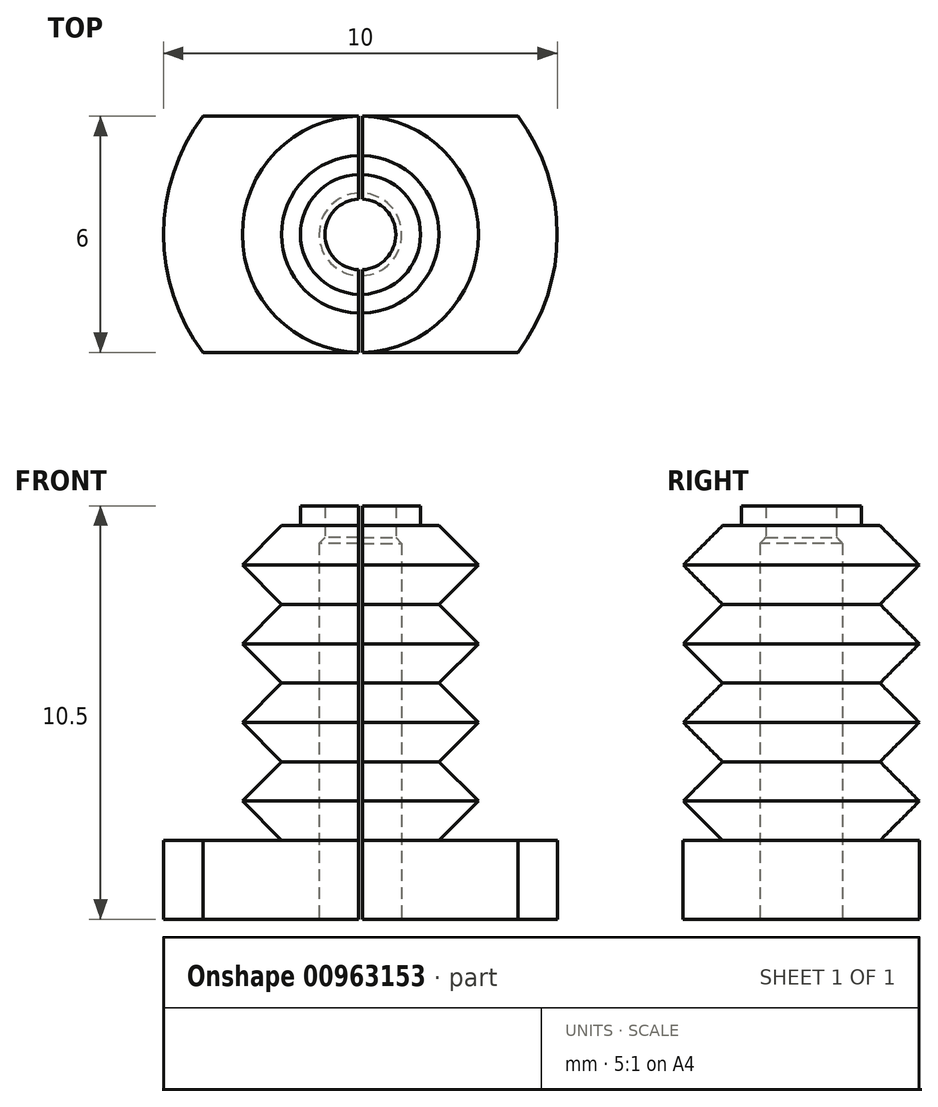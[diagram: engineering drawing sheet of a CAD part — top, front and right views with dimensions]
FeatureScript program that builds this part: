
annotation { "Feature Type Name" : "Feature", "Feature Type Description" : "" }
export const myFeature = defineFeature(function(context is Context, id is Id, definition is map)
    precondition{}
    {
        {
            var Q0;
            Q0=qCreatedBy(makeId("Top.planeOp"),FACE);
            var sketch = newSketch(context, id + "F0", { "sketchPlane" : qUnion([Q0])});
            skArc(sketch, "E0", {"start": v(0.12, 1.04) * mm, "mid": v(-1.05, 0) * mm, "end": v(0.12, -1.04) * mm});
            skArc(sketch, "E1", {"start": v(-0.16, 2) * mm, "mid": v(-2, 0) * mm, "end": v(-0.16, -2) * mm});
            skArc(sketch, "E2.trimOffspring", {"start": v(0.12, -1.04) * mm, "mid": v(1.05, 0) * mm, "end": v(0.12, 1.04) * mm});
            skArc(sketch, "E3.trimOffspring", {"start": v(-0.16, -2) * mm, "mid": v(2, 0) * mm, "end": v(-0.16, 2) * mm});
            skSolve(sketch);
        }
        {
            var Q0;
            Q0=makeQuery(id+"F0.imprint","IMPRINT",FACE,{"disambiguationData":[TD([[makeQuery(id+"F0.imprint","IMPRINT",EDGE,{"derivedFrom":sQuery(id+"F0.wireOp",EDGE,"E0")}),-1.0]])]});
            extrude(context, id + "F1", {"entities" : qUnion([Q0]), "depth" : 10 * mm, "offsetDistance" : 25 * mm});
        }
        {
            var Q0;
            Q0=qCreatedBy(makeId("Right.planeOp"),FACE);
            var sketch = newSketch(context, id + "F2", { "sketchPlane" : qUnion([Q0])});
            skLineSegment(sketch, "E4", {"start": v(-2, 8) * mm, "end": v(-3, 7) * mm});
            skLineSegment(sketch, "E5", {"start": v(-3, 7) * mm, "end": v(-2, 6) * mm});
            skLineSegment(sketch, "E6", {"start": v(-2, 6) * mm, "end": v(-3, 5) * mm});
            skLineSegment(sketch, "E7", {"start": v(-3, 5) * mm, "end": v(-2, 4) * mm});
            skLineSegment(sketch, "E8", {"start": v(-2, 4) * mm, "end": v(-3, 3) * mm});
            skLineSegment(sketch, "E9", {"start": v(-3, 3) * mm, "end": v(-2, 2) * mm});
            skLineSegment(sketch, "E10", {"start": v(0, 15.2) * mm, "end": v(0, -5.46) * mm});
            skLineSegment(sketch, "E11", {"start": v(-2, 10) * mm, "end": v(-2, 0) * mm});
            skLineSegment(sketch, "E12", {"start": v(-2, 8) * mm, "end": v(-3, 9) * mm});
            skLineSegment(sketch, "E13", {"start": v(-3, 9) * mm, "end": v(-2, 10) * mm});
            skLineSegment(sketch, "E14", {"start": v(-2, 2) * mm, "end": v(-5, 2) * mm});
            skLineSegment(sketch, "E15", {"start": v(-5, 2) * mm, "end": v(-5, 0) * mm});
            skLineSegment(sketch, "E16", {"start": v(-5, 0) * mm, "end": v(-2, 0) * mm});
            skSolve(sketch);
        }
        {
            var Q0;
            Q0 = qSketchRegion(id + "F2", true);
            var Q1;
            Q1=sQuery(id+"F2.wireOp",EDGE,"E10");
            revolve(context, id + "F3", {"operationType" : NewBodyOperationType.ADD, "surfaceOperationType" : NewSurfaceOperationType.NEW, "entities" : qUnion([Q0]), "axis" : qUnion([Q1]), "revolveType" : RevolveType.FULL});
        }
        {
            var Q0;
            Q0=makeQuery(id+"F3.boolean.opBoolean","MERGE",FACE,{"derivedFrom":[makeQuery(id+"F1.opExtrude","CAP_FACE",FACE,{"disambiguationData":[OSD([sQuery(id+"F0.wireOp",EDGE,"E0"),sQuery(id+"F0.wireOp",EDGE,"E1"),sQuery(id+"F0.wireOp",EDGE,"E2.trimOffspring"),sQuery(id+"F0.wireOp",EDGE,"E3.trimOffspring")])],"isStart":true}),makeQuery(id+"F3.opRevolve","SWEPT_FACE",FACE,{"disambiguationData":[OSD([sQuery(id+"F2.wireOp",EDGE,"E16")])]})]});
            var sketch = newSketch(context, id + "F4", { "sketchPlane" : qUnion([Q0])});
            skLineSegment(sketch, "E17.bottom", {"start": v(0.05, 15) * mm, "end": v(-0.05, 15) * mm});
            skLineSegment(sketch, "E17.top", {"start": v(0.05, -15) * mm, "end": v(-0.05, -15) * mm});
            skLineSegment(sketch, "E17.left", {"start": v(0.05, 15) * mm, "end": v(0.05, -15) * mm});
            skLineSegment(sketch, "E17.right", {"start": v(-0.05, 15) * mm, "end": v(-0.05, -15) * mm});
            skPoint(sketch, "E17.middle", {"position": v(0, 0) * mm});
            skLineSegment(sketch, "E18", {"start": v(-4, 3) * mm, "end": v(4, 3) * mm});
            skLineSegment(sketch, "E19.MirrorCS", {"start": v(-4, -3) * mm, "end": v(4, -3) * mm});
            skSolve(sketch);
        }
        {
            var Q0;
            {var subQ0=sQuery(id+"F4.wireOp",EDGE,"14083dd1-1344-4e08-bf10-f83d3822586a0.MirrorCS");Q0=makeQuery(id+"F4.imprint","IMPRINT",FACE,{"disambiguationData":[TD([[makeQuery(id+"F4.imprint","IMPRINT",EDGE,{"derivedFrom":subQ0}),1.0]])]});}
            var Q1;
            {var subQ0=sQuery(id+"F4.wireOp",EDGE,"waH5iUfG-ntGH-ufo2-9Cgk-GyOwy1ScrqeD");Q1=makeQuery(id+"F4.imprint","IMPRINT",FACE,{"disambiguationData":[TD([[makeQuery(id+"F4.imprint","IMPRINT",EDGE,{"derivedFrom":subQ0}),-1.0]])]});}
            var Q2;
            {var subQ0=sQuery(id+"F4.wireOp",EDGE,"E18");var subQ1=sQuery(id+"F4.wireOp",EDGE,"E17.right");var subQ2=makeQuery(id+"F4.imprint","INTERSECT",VERTEX,{"derivedFrom":[subQ1,subQ0]});Q2=makeQuery(id+"F4.imprint","IMPRINT",FACE,{"disambiguationData":[TD([[makeQuery(id+"F4.imprint","IMPRINT",EDGE,{"disambiguationData":[TD([[subQ2,1.0]])],"derivedFrom":subQ1}),-1.0]])]});}
            var Q3;
            {var subQ0=sQuery(id+"F4.wireOp",EDGE,"E18");var subQ1=sQuery(id+"F4.wireOp",EDGE,"E17.left");var subQ2=makeQuery(id+"F4.imprint","INTERSECT",VERTEX,{"derivedFrom":[subQ1,subQ0]});Q3=makeQuery(id+"F4.imprint","IMPRINT",FACE,{"disambiguationData":[TD([[makeQuery(id+"F4.imprint","IMPRINT",EDGE,{"disambiguationData":[TD([[subQ2,1.0]])],"derivedFrom":subQ1}),1.0]])]});}
            var Q4;
            {var subQ0=sQuery(id+"F4.wireOp",EDGE,"E19.MirrorCS");var subQ1=sQuery(id+"F4.wireOp",EDGE,"E17.right");var subQ2=makeQuery(id+"F4.imprint","INTERSECT",VERTEX,{"derivedFrom":[subQ1,subQ0]});Q4=makeQuery(id+"F4.imprint","IMPRINT",FACE,{"disambiguationData":[TD([[makeQuery(id+"F4.imprint","IMPRINT",EDGE,{"disambiguationData":[TD([[subQ2,-1.0]])],"derivedFrom":subQ1}),-1.0]])]});}
            var Q5;
            {var subQ0=sQuery(id+"F4.wireOp",EDGE,"E19.MirrorCS");var subQ1=sQuery(id+"F4.wireOp",EDGE,"E17.left");var subQ2=makeQuery(id+"F4.imprint","INTERSECT",VERTEX,{"derivedFrom":[subQ1,subQ0]});Q5=makeQuery(id+"F4.imprint","IMPRINT",FACE,{"disambiguationData":[TD([[makeQuery(id+"F4.imprint","IMPRINT",EDGE,{"disambiguationData":[TD([[subQ2,-1.0]])],"derivedFrom":subQ1}),1.0]])]});}
            var Q6;
            {var subQ0=sQuery(id+"F4.wireOp",EDGE,"E17.bottom");Q6=makeQuery(id+"F4.imprint","IMPRINT",FACE,{"disambiguationData":[TD([[makeQuery(id+"F4.imprint","IMPRINT",EDGE,{"derivedFrom":subQ0}),1.0]])]});}
            var Q7;
            {var subQ0=sQuery(id+"F4.wireOp",EDGE,"E17.top");Q7=makeQuery(id+"F4.imprint","IMPRINT",FACE,{"disambiguationData":[TD([[makeQuery(id+"F4.imprint","IMPRINT",EDGE,{"derivedFrom":subQ0}),-1.0]])]});}
            var Q8;
            {var subQ0=sQuery(id+"F4.wireOp",EDGE,"E18");var subQ1=sQuery(id+"F4.wireOp",EDGE,"E17.left");var subQ2=makeQuery(id+"F4.imprint","INTERSECT",VERTEX,{"derivedFrom":[subQ1,subQ0]});Q8=makeQuery(id+"F4.imprint","IMPRINT",FACE,{"disambiguationData":[TD([[makeQuery(id+"F4.imprint","IMPRINT",EDGE,{"disambiguationData":[TD([[subQ2,1.0]])],"derivedFrom":subQ0}),-1.0]])]});}
            var Q9;
            {var subQ0=sQuery(id+"F4.wireOp",EDGE,"E19.MirrorCS");var subQ1=sQuery(id+"F4.wireOp",EDGE,"E17.left");var subQ2=makeQuery(id+"F4.imprint","INTERSECT",VERTEX,{"derivedFrom":[subQ1,subQ0]});Q9=makeQuery(id+"F4.imprint","IMPRINT",FACE,{"disambiguationData":[TD([[makeQuery(id+"F4.imprint","IMPRINT",EDGE,{"disambiguationData":[TD([[subQ2,1.0]])],"derivedFrom":subQ0}),1.0]])]});}
            var Q10;
            {var subQ0=sQuery(id+"F4.wireOp",EDGE,"E19.MirrorCS");var subQ1=sQuery(id+"F4.wireOp",EDGE,"E17.left");var subQ2=makeQuery(id+"F4.imprint","INTERSECT",VERTEX,{"derivedFrom":[subQ1,subQ0]});Q10=makeQuery(id+"F4.imprint","IMPRINT",FACE,{"disambiguationData":[TD([[makeQuery(id+"F4.imprint","IMPRINT",EDGE,{"disambiguationData":[TD([[subQ2,1.0]])],"derivedFrom":subQ0}),-1.0]])]});}
            var Q11;
            {var subQ0=sQuery(id+"F4.wireOp",EDGE,"E17.left");var subQ1=makeQuery(id+"F1.opExtrude","CAP_EDGE",EDGE,{"disambiguationData":[OSD([sQuery(id+"F0.wireOp",EDGE,"E0"),sQuery(id+"F0.wireOp",EDGE,"E2.trimOffspring")])],"isStart":true});var subQ2=makeQuery(id+"F4.imprint","INTERSECT",VERTEX,{"disambiguationData":[OD(0.0)],"derivedFrom":[subQ1,subQ0]});Q11=makeQuery(id+"F4.imprint","IMPRINT",FACE,{"disambiguationData":[TD([[makeQuery(id+"F4.imprint","IMPRINT",EDGE,{"disambiguationData":[TD([[subQ2,-1.0]])],"derivedFrom":subQ0}),-1.0]])]});}
            var Q12;
            {var subQ0=sQuery(id+"F4.wireOp",EDGE,"E18");var subQ1=sQuery(id+"F4.wireOp",EDGE,"E17.left");var subQ2=makeQuery(id+"F4.imprint","INTERSECT",VERTEX,{"derivedFrom":[subQ1,subQ0]});Q12=makeQuery(id+"F4.imprint","IMPRINT",FACE,{"disambiguationData":[TD([[makeQuery(id+"F4.imprint","IMPRINT",EDGE,{"disambiguationData":[TD([[subQ2,1.0]])],"derivedFrom":subQ0}),1.0]])]});}
            extrude(context, id + "F5", {"entities" : qUnion([Q0, Q1, Q2, Q3, Q4, Q5, Q6, Q7, Q8, Q9, Q10, Q11, Q12]), "operationType" : NewBodyOperationType.REMOVE, "endBound" : BoundingType.THROUGH_ALL, "oppositeDirection" : true, "depth" : 25 * mm, "offsetDistance" : 25 * mm});
        }
        {
            var Q0;
            {var subQ0=sQuery(id+"F0.wireOp",EDGE,"E2.trimOffspring");var subQ1=sQuery(id+"F0.wireOp",EDGE,"E0");var subQ2=sQuery(id+"F0.wireOp",EDGE,"E3.trimOffspring");var subQ3=sQuery(id+"F0.wireOp",EDGE,"E1");var subQ4=sQuery(id+"F4.wireOp",EDGE,"E17.right");var subQ5=makeQuery(id+"F1.opExtrude","CAP_EDGE",EDGE,{"disambiguationData":[OSD([subQ1,subQ0])],"isStart":true});var subQ7=makeQuery(id+"F4.imprint","INTERSECT",VERTEX,{"disambiguationData":[OD(0.0)],"derivedFrom":[subQ5,subQ4]});Q0=makeQuery(id+"F5.boolean.opBoolean","SPLIT",FACE,{"disambiguationData":[TD([makeQuery(id+"F5.opExtrude","SWEPT_FACE",FACE,{"disambiguationData":[OSD([subQ4]),TDD([makeQuery(id+"F4.imprint","IMPRINT",EDGE,{"disambiguationData":[TD([[makeQuery(id+"F4.imprint","INTERSECT",VERTEX,{"derivedFrom":[subQ4,sQuery(id+"F4.wireOp",EDGE,"E18")]}),-1.0]])],"derivedFrom":subQ4}),makeQuery(id+"F4.imprint","IMPRINT",EDGE,{"disambiguationData":[TD([[subQ7,-1.0]])],"derivedFrom":subQ4}),makeQuery(id+"F4.imprint","IMPRINT",EDGE,{"disambiguationData":[TD([[makeQuery(id+"F4.imprint","INTERSECT",VERTEX,{"derivedFrom":[subQ4,sQuery(id+"F4.wireOp",EDGE,"E19.MirrorCS")]}),1.0]])],"derivedFrom":subQ4})])]})])],"derivedFrom":makeQuery(id+"F1.opExtrude","CAP_FACE",FACE,{"disambiguationData":[OSD([subQ1,subQ3,subQ0,subQ2])],"isStart":false})});}
            var sketch = newSketch(context, id + "F6", { "sketchPlane" : qUnion([Q0])});
            skArc(sketch, "E20", {"start": v(-0.05, 0.9) * mm, "mid": v(-0.9, 0) * mm, "end": v(-0.05, -0.9) * mm});
            skArc(sketch, "E21", {"start": v(-0.05, -1.52) * mm, "mid": v(-1.52, 0) * mm, "end": v(-0.05, 1.52) * mm});
            skLineSegment(sketch, "E22", {"start": v(-0.05, -1.52) * mm, "end": v(-0.05, -0.9) * mm});
            skLineSegment(sketch, "E23", {"start": v(-0.05, 1.52) * mm, "end": v(-0.05, 0.9) * mm});
            skArc(sketch, "E24.MirrorCS", {"start": v(0.05, 0.9) * mm, "mid": v(0.9, 0) * mm, "end": v(0.05, -0.9) * mm});
            skLineSegment(sketch, "E25.MirrorCS", {"start": v(0.05, 1.52) * mm, "end": v(0.05, 0.9) * mm});
            skArc(sketch, "E26.MirrorCS", {"start": v(0.05, -1.52) * mm, "mid": v(1.52, 0) * mm, "end": v(0.05, 1.52) * mm});
            skLineSegment(sketch, "E27.MirrorCS", {"start": v(0.05, -1.52) * mm, "end": v(0.05, -0.9) * mm});
            skSolve(sketch);
        }
        {
            var Q0;
            Q0 = qSketchRegion(id + "F6", true);
            extrude(context, id + "F7", {"entities" : qUnion([Q0]), "operationType" : NewBodyOperationType.ADD, "endBound" : BoundingType.SYMMETRIC, "depth" : 1 * mm, "offsetDistance" : 25 * mm});
        }
        {
            var Q0;
            Q0=makeQuery(id+"F7.opExtrude","CAP_EDGE",EDGE,{"disambiguationData":[OSD([sQuery(id+"F6.wireOp",EDGE,"E20")])],"isStart":true});
            var Q1;
            Q1=makeQuery(id+"F7.opExtrude","CAP_EDGE",EDGE,{"disambiguationData":[OSD([sQuery(id+"F6.wireOp",EDGE,"E24.MirrorCS")])],"isStart":true});
            chamfer(context, id + "F8", {"entities" : qUnion([Q0, Q1]), "width" : 0.2 * mm, "tangentPropagation" : true});
        }
    });
